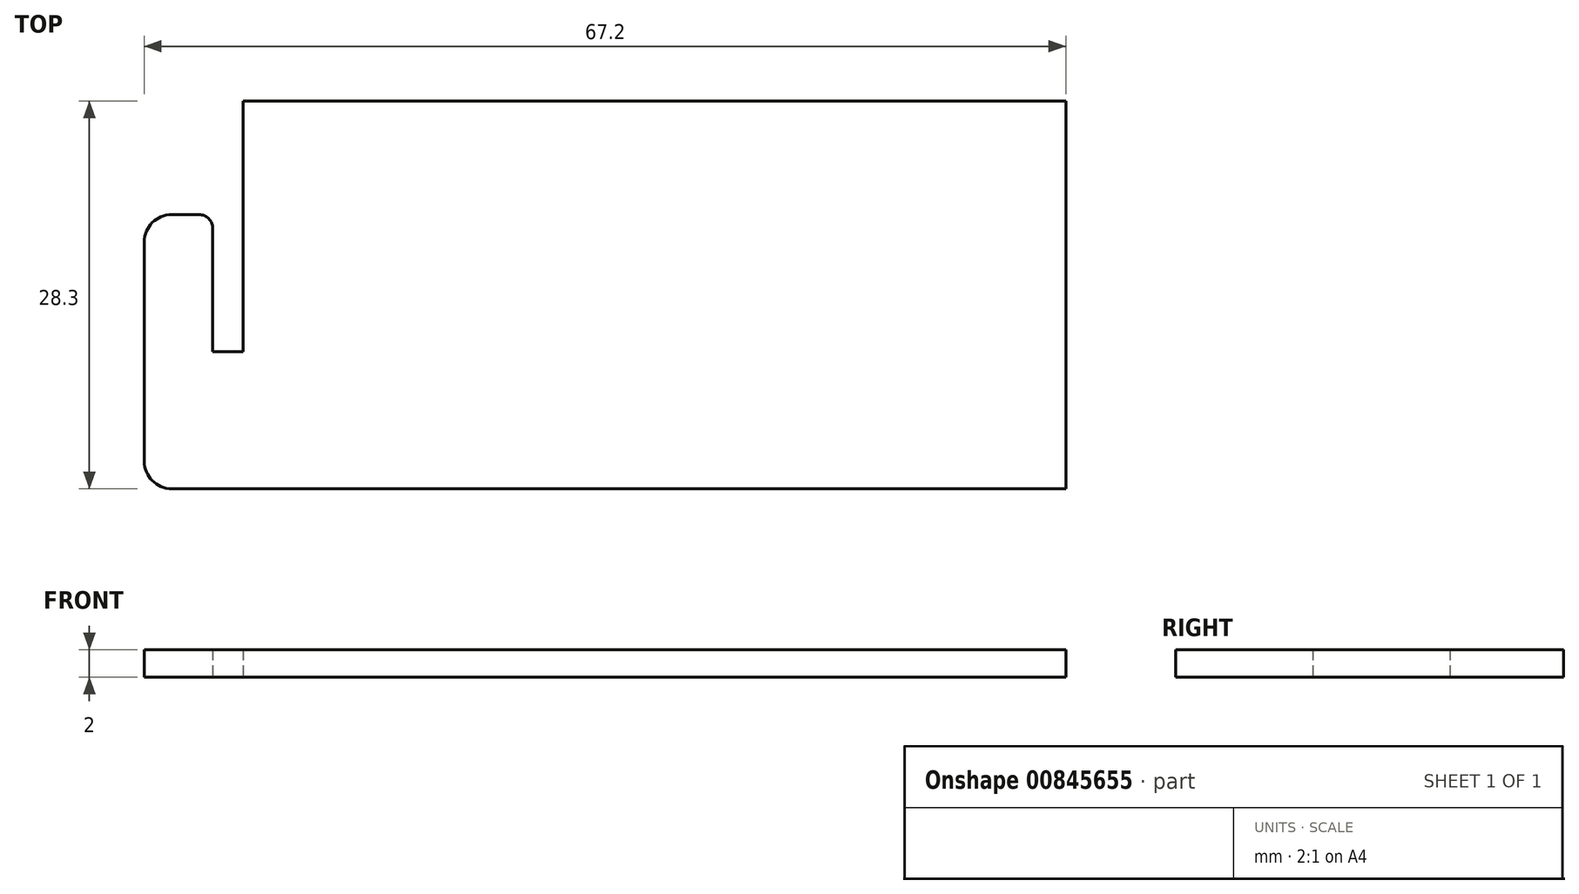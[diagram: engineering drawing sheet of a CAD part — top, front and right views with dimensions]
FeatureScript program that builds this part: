
annotation { "Feature Type Name" : "Feature", "Feature Type Description" : "" }
export const myFeature = defineFeature(function(context is Context, id is Id, definition is map)
    precondition{}
    {
        {
            var Q0;
            Q0=qCreatedBy(makeId("Top.planeOp"),FACE);
            var sketch = newSketch(context, id + "F0", { "sketchPlane" : qUnion([Q0])});
            skLineSegment(sketch, "E0.bottom", {"start": v(-59.96, 7.43) * mm, "end": v(0.04, 7.43) * mm});
            skLineSegment(sketch, "E0.top", {"start": v(-59.96, -20.87) * mm, "end": v(0.04, -20.87) * mm});
            skLineSegment(sketch, "E0.left", {"start": v(-59.96, 7.43) * mm, "end": v(-59.96, -20.87) * mm});
            skLineSegment(sketch, "E0.right", {"start": v(0.04, 7.43) * mm, "end": v(0.04, -20.87) * mm});
            skLineSegment(sketch, "E1", {"start": v(-65.16, -0.87) * mm, "end": v(-63.18, -0.87) * mm});
            skLineSegment(sketch, "E2", {"start": v(-62.16, -1.89) * mm, "end": v(-62.16, -10.87) * mm});
            skPoint(sketch, "E2.endSnap0", {"position": v(-63.57, -10.87) * mm});
            skLineSegment(sketch, "E3", {"start": v(-62.16, -10.87) * mm, "end": v(-59.96, -10.87) * mm});
            skLineSegment(sketch, "E4", {"start": v(-59.96, -10.87) * mm, "end": v(-59.96, -20.87) * mm});
            skLineSegment(sketch, "E5", {"start": v(-59.96, -20.87) * mm, "end": v(-62.16, -20.87) * mm});
            skLineSegment(sketch, "E6", {"start": v(-62.16, -20.87) * mm, "end": v(-65.16, -20.87) * mm});
            skLineSegment(sketch, "E7", {"start": v(-67.16, -18.87) * mm, "end": v(-67.16, -2.87) * mm});
            skPoint(sketch, "E8.visualSharp", {"position": v(-62.16, -0.87) * mm});
            skArc(sketch, "E8.filletArc", {"start": v(-62.16, -1.89) * mm, "mid": v(-62.46, -1.17) * mm, "end": v(-63.18, -0.87) * mm});
            skPoint(sketch, "E9.visualSharp", {"position": v(-67.16, -0.87) * mm});
            skArc(sketch, "E9.filletArc", {"start": v(-65.16, -0.87) * mm, "mid": v(-66.58, -1.45) * mm, "end": v(-67.16, -2.87) * mm});
            skPoint(sketch, "E10.visualSharp", {"position": v(-67.16, -20.87) * mm});
            skArc(sketch, "E10.filletArc", {"start": v(-67.16, -18.87) * mm, "mid": v(-66.58, -20.28) * mm, "end": v(-65.16, -20.87) * mm});
            skLineSegment(sketch, "E11", {"start": v(-29.96, 13.29) * mm, "end": v(-29.96, -22.7) * mm, "construction": true});
            skArc(sketch, "E12.MirrorCS", {"start": v(2.24, -1.89) * mm, "mid": v(2.54, -1.17) * mm, "end": v(3.26, -0.87) * mm});
            skLineSegment(sketch, "E13.MirrorCS", {"start": v(0.04, -10.87) * mm, "end": v(0.04, -20.87) * mm});
            skArc(sketch, "E14.MirrorCS", {"start": v(7.24, -18.87) * mm, "mid": v(6.65, -20.28) * mm, "end": v(5.24, -20.87) * mm});
            skPoint(sketch, "E15.MirrorP", {"position": v(7.24, -20.87) * mm});
            skPoint(sketch, "E16.MirrorP", {"position": v(2.24, -0.87) * mm});
            skPoint(sketch, "E17.MirrorP", {"position": v(7.24, -0.87) * mm});
            skArc(sketch, "E18.MirrorCS", {"start": v(5.24, -0.87) * mm, "mid": v(6.65, -1.45) * mm, "end": v(7.24, -2.87) * mm});
            skLineSegment(sketch, "E19.MirrorCS", {"start": v(2.24, -1.89) * mm, "end": v(2.24, -10.87) * mm});
            skPoint(sketch, "E20.MirrorP", {"position": v(3.65, -10.87) * mm});
            skLineSegment(sketch, "E21.MirrorCS", {"start": v(7.24, -18.87) * mm, "end": v(7.24, -2.87) * mm});
            skLineSegment(sketch, "E22.MirrorCS", {"start": v(0.04, -20.87) * mm, "end": v(2.24, -20.87) * mm});
            skLineSegment(sketch, "E23.MirrorCS", {"start": v(5.24, -0.87) * mm, "end": v(3.26, -0.87) * mm});
            skLineSegment(sketch, "E24.MirrorCS", {"start": v(2.24, -10.87) * mm, "end": v(0.04, -10.87) * mm});
            skLineSegment(sketch, "E25.MirrorCS", {"start": v(2.24, -20.87) * mm, "end": v(5.24, -20.87) * mm});
            skSolve(sketch);
        }
        {
            var Q0;
            {var subQ6=sQuery(id+"F0.wireOp",EDGE,"E0.bottom");Q0=qUnion([makeQuery(id+"F0.imprint","IMPRINT",FACE,{"disambiguationData":[TD([[makeQuery(id+"F0.imprint","IMPRINT",EDGE,{"derivedFrom":sQuery(id+"F0.wireOp",EDGE,"E1")}),-1.0]])]}),makeQuery(id+"F0.imprint","IMPRINT",FACE,{"disambiguationData":[TD([[makeQuery(id+"F0.imprint","IMPRINT",EDGE,{"derivedFrom":sQuery(id+"F0.wireOp",EDGE,"E12.MirrorCS")}),-1.0]])]}),makeQuery(id+"F0.imprint","IMPRINT",FACE,{"disambiguationData":[TD([[makeQuery(id+"F0.imprint","IMPRINT",EDGE,{"derivedFrom":subQ6}),-1.0]])]})]);}
            extrude(context, id + "F1", {"entities" : qUnion([Q0]), "depth" : 2 * mm, "offsetDistance" : 25 * mm});
        }
    });
